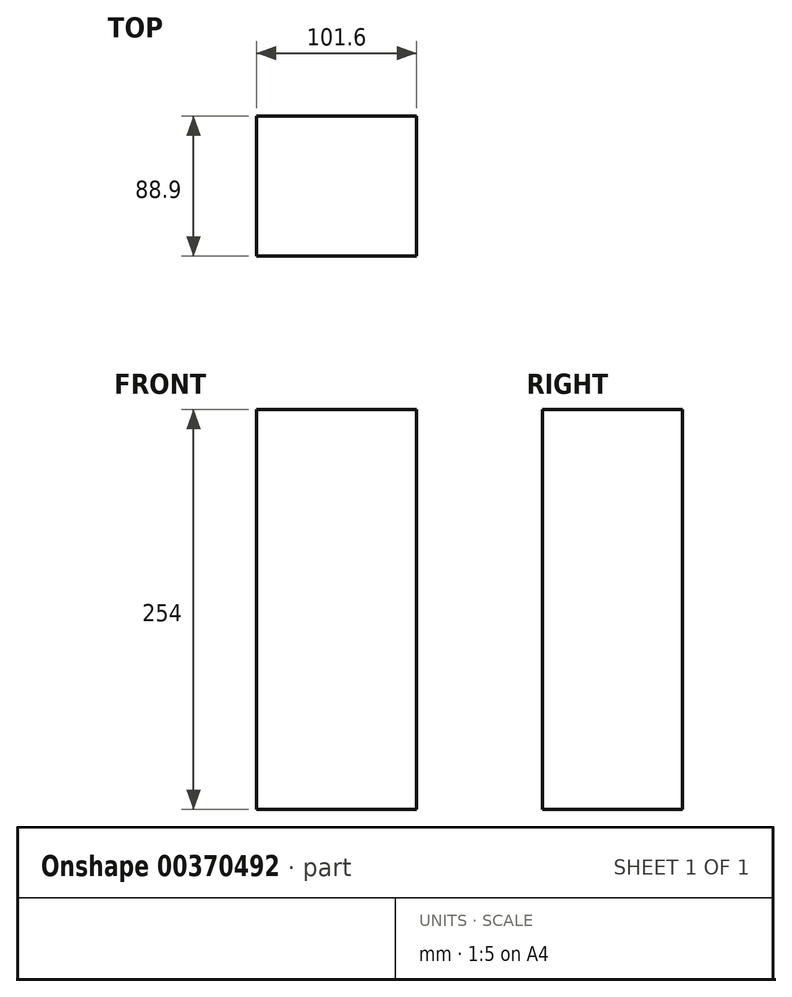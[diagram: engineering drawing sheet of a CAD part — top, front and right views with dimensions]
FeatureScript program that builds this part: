
annotation { "Feature Type Name" : "Feature", "Feature Type Description" : "" }
export const myFeature = defineFeature(function(context is Context, id is Id, definition is map)
    precondition{}
    {
        {
            var Q0;
            Q0=qCreatedBy(makeId("Top.planeOp"),FACE);
            var sketch = newSketch(context, id + "F0", { "sketchPlane" : qUnion([Q0])});
            skLineSegment(sketch, "E0.bottom", {"start": v(-50.8, 44.45) * mm, "end": v(50.8, 44.45) * mm});
            skLineSegment(sketch, "E0.top", {"start": v(-50.8, -44.45) * mm, "end": v(50.8, -44.45) * mm});
            skLineSegment(sketch, "E0.left", {"start": v(-50.8, 44.45) * mm, "end": v(-50.8, -44.45) * mm});
            skLineSegment(sketch, "E0.right", {"start": v(50.8, 44.45) * mm, "end": v(50.8, -44.45) * mm});
            skPoint(sketch, "E0.middle", {"position": v(0, 0) * mm});
            skSolve(sketch);
        }
        {
            var Q0;
            Q0=makeQuery(id+"F0.imprint","IMPRINT",FACE,{"disambiguationData":[TD([[makeQuery(id+"F0.imprint","IMPRINT",EDGE,{"derivedFrom":sQuery(id+"F0.wireOp",EDGE,"E0.bottom")}),-1.0]])]});
            extrude(context, id + "F1", {"entities" : qUnion([Q0]), "depth" : 254 * mm});
        }
    });
